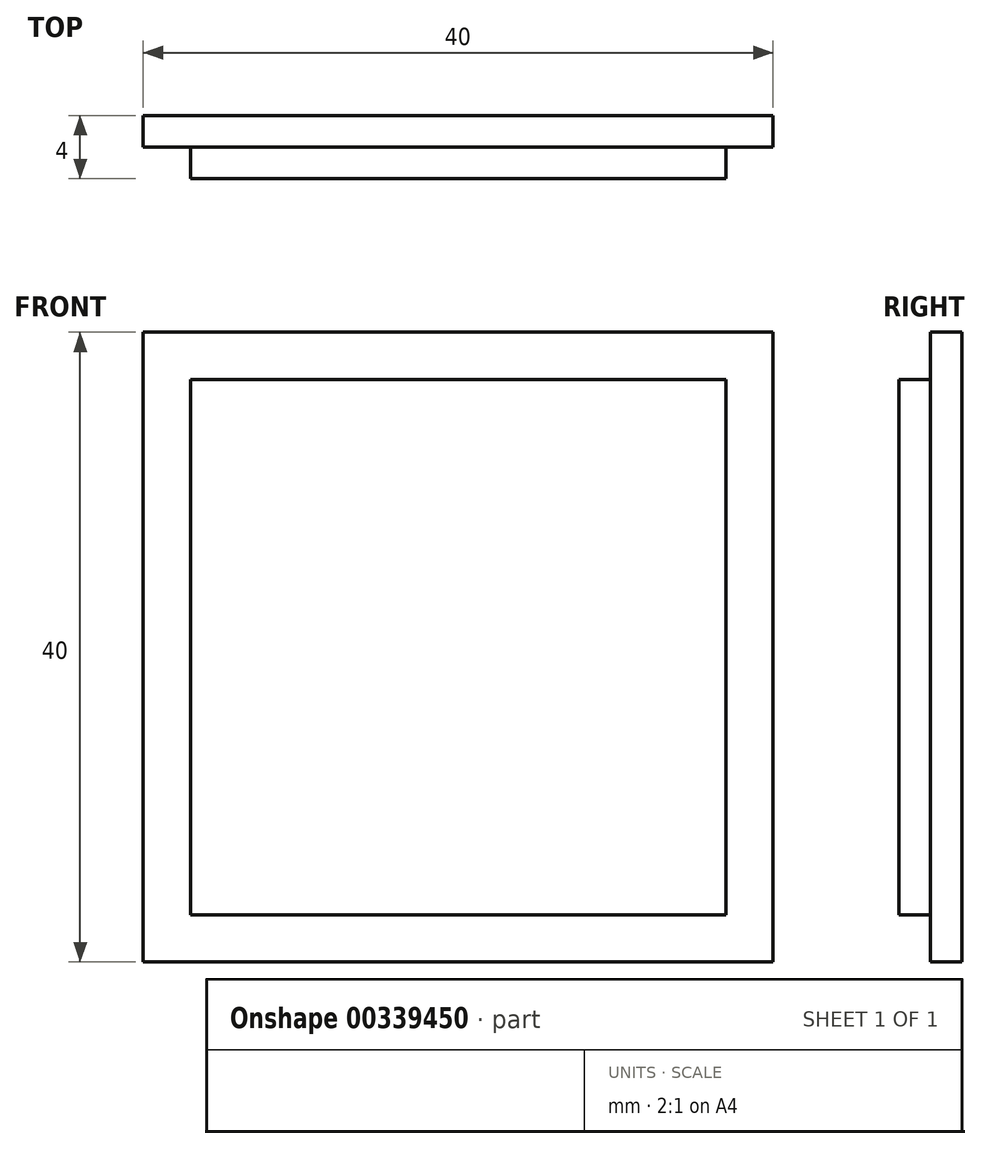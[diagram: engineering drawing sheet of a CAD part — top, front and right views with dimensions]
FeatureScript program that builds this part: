
annotation { "Feature Type Name" : "Feature", "Feature Type Description" : "" }
export const myFeature = defineFeature(function(context is Context, id is Id, definition is map)
    precondition{}
    {
        {
            var Q0;
            Q0=qCreatedBy(makeId("Front.planeOp"),FACE);
            var sketch = newSketch(context, id + "F0", { "sketchPlane" : qUnion([Q0])});
            skLineSegment(sketch, "E0.bottom", {"start": v(20, -20) * mm, "end": v(-20, -20) * mm});
            skLineSegment(sketch, "E0.top", {"start": v(20, 20) * mm, "end": v(-20, 20) * mm});
            skLineSegment(sketch, "E0.left", {"start": v(20, -20) * mm, "end": v(20, 20) * mm});
            skLineSegment(sketch, "E0.right", {"start": v(-20, -20) * mm, "end": v(-20, 20) * mm});
            skPoint(sketch, "E0.middle", {"position": v(0, 0) * mm});
            skLineSegment(sketch, "E1.bottom", {"start": v(17, -17) * mm, "end": v(-17, -17) * mm});
            skLineSegment(sketch, "E1.top", {"start": v(17, 17) * mm, "end": v(-17, 17) * mm});
            skLineSegment(sketch, "E1.left", {"start": v(17, -17) * mm, "end": v(17, 17) * mm});
            skLineSegment(sketch, "E1.right", {"start": v(-17, -17) * mm, "end": v(-17, 17) * mm});
            skSolve(sketch);
        }
        {
            var Q0;
            Q0=makeQuery(id+"F0.imprint","IMPRINT",FACE,{"disambiguationData":[TD([[makeQuery(id+"F0.imprint","IMPRINT",EDGE,{"derivedFrom":sQuery(id+"F0.wireOp",EDGE,"E1.bottom")}),-1.0]])]});
            extrude(context, id + "F1", {"entities" : qUnion([Q0]), "depth" : 4 * mm});
        }
        {
            var Q0;
            Q0=qCreatedBy(makeId("Front.planeOp"),FACE);
            var sketch = newSketch(context, id + "F2", { "sketchPlane" : qUnion([Q0])});
            skLineSegment(sketch, "E2.bottom", {"start": v(20, -20) * mm, "end": v(-20, -20) * mm});
            skLineSegment(sketch, "E2.top", {"start": v(20, 20) * mm, "end": v(-20, 20) * mm});
            skLineSegment(sketch, "E2.left", {"start": v(20, -20) * mm, "end": v(20, 20) * mm});
            skLineSegment(sketch, "E2.right", {"start": v(-20, -20) * mm, "end": v(-20, 20) * mm});
            skPoint(sketch, "E2.middle", {"position": v(0, 0) * mm});
            skSolve(sketch);
        }
        {
            var Q0;
            Q0=makeQuery(id+"F2.imprint","IMPRINT",FACE,{"disambiguationData":[TD([[makeQuery(id+"F2.imprint","IMPRINT",EDGE,{"derivedFrom":sQuery(id+"F2.wireOp",EDGE,"E2.bottom")}),-1.0]])]});
            extrude(context, id + "F3", {"entities" : qUnion([Q0]), "operationType" : NewBodyOperationType.ADD, "depth" : 2 * mm});
        }
    });
